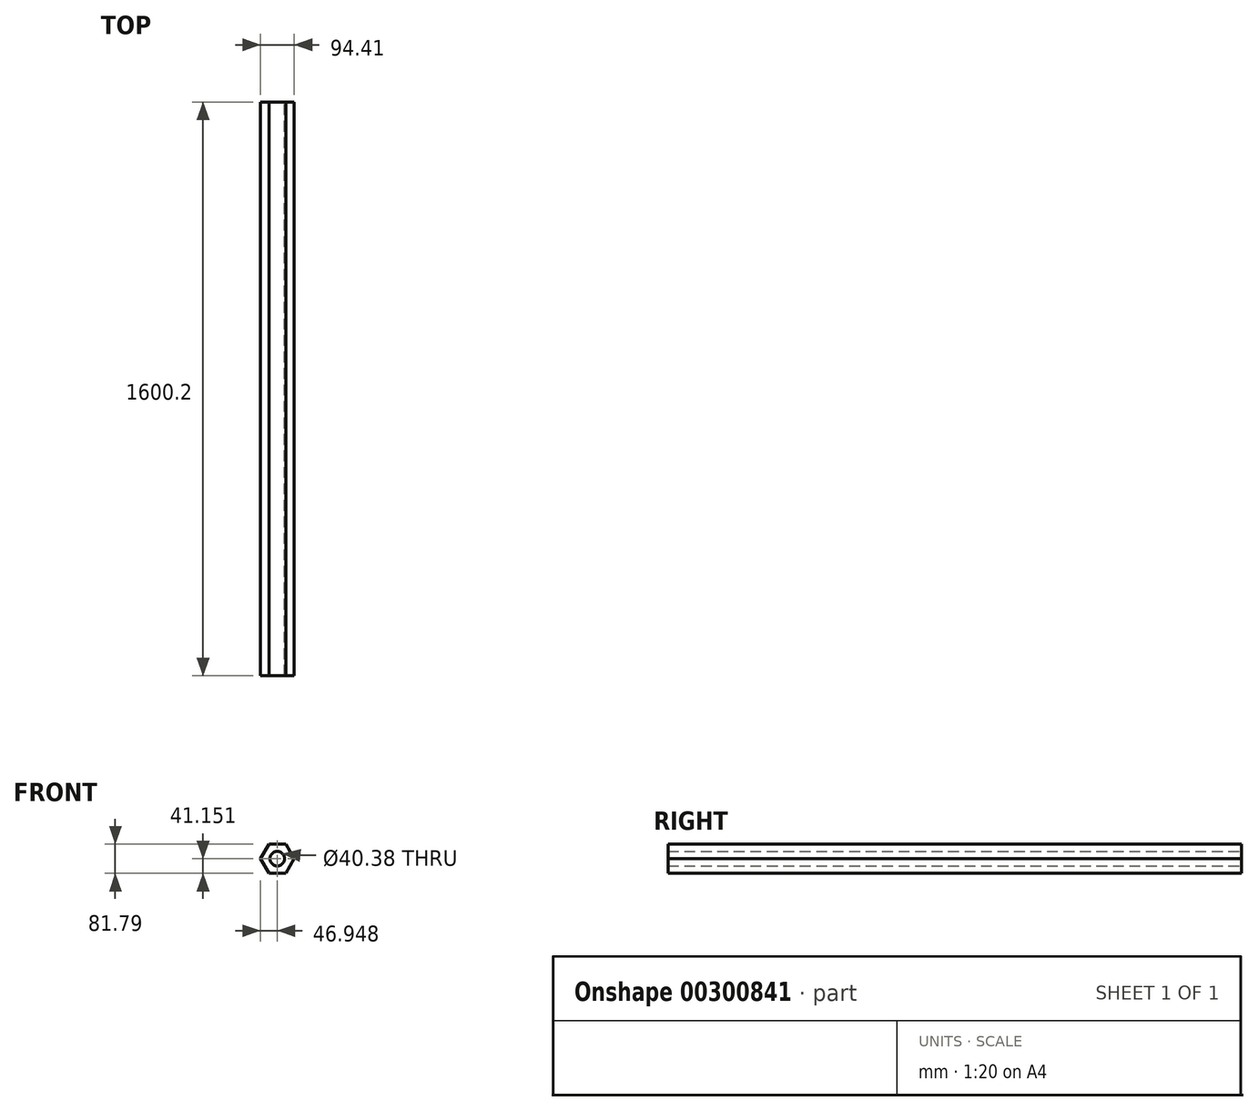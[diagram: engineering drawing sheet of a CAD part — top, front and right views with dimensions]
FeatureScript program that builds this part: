
annotation { "Feature Type Name" : "Feature", "Feature Type Description" : "" }
export const myFeature = defineFeature(function(context is Context, id is Id, definition is map)
    precondition{}
    {
        {
            var Q0;
            Q0=qCreatedBy(makeId("Front.planeOp"),FACE);
            var sketch = newSketch(context, id + "F0", { "sketchPlane" : qUnion([Q0])});
            skCircle(sketch, "E0.cCircle", {"center": v(0.52, -0.39) * mm, "radius": 40.88 * mm, "construction": true});
            skLineSegment(sketch, "E0.0", {"start": v(24.14, 40.48) * mm, "end": v(47.72, -0.41) * mm});
            skLineSegment(sketch, "E0.1", {"start": v(47.72, -0.41) * mm, "end": v(24.1, -41.28) * mm});
            skLineSegment(sketch, "E0.2", {"start": v(24.1, -41.28) * mm, "end": v(-23.1, -41.26) * mm});
            skLineSegment(sketch, "E0.3", {"start": v(-23.1, -41.26) * mm, "end": v(-46.7, -0.36) * mm});
            skLineSegment(sketch, "E0.4", {"start": v(-46.7, -0.36) * mm, "end": v(-23.06, 40.5) * mm});
            skLineSegment(sketch, "E0.5", {"start": v(-23.06, 40.5) * mm, "end": v(24.14, 40.48) * mm});
            skPoint(sketch, "E0.0.midPoint", {"position": v(35.93, 20.03) * mm});
            skCircle(sketch, "E1", {"center": v(0.26, -0.13) * mm, "radius": 20.2 * mm});
            skSolve(sketch);
        }
        {
            var Q0;
            Q0=makeQuery(id+"F0.imprint","IMPRINT",FACE,{"disambiguationData":[TD([[makeQuery(id+"F0.imprint","IMPRINT",EDGE,{"derivedFrom":sQuery(id+"F0.wireOp",EDGE,"E0.0")}),-1.0]])]});
            extrude(context, id + "F1", {"entities" : qUnion([Q0]), "depth" : 1600.2 * mm});
        }
    });
